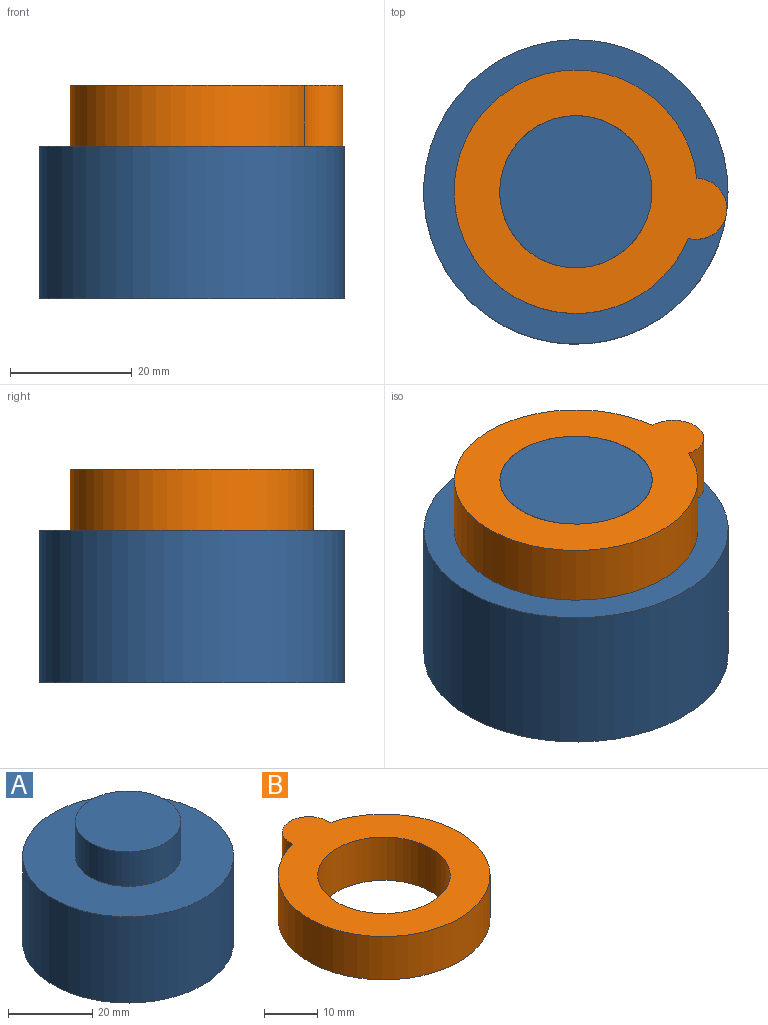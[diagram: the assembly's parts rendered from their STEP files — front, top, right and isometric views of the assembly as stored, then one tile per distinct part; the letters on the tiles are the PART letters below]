
ASSEMBLY  parts=2 mates=1
PART A: 5 faces, bbox 50x50x35 mm
  f0: cylinder r=25mm len=50mm, axis (0,0,-1), area 3927mm2, adj f1,f2
  f1: plane 50x50mm, normal (0,0,1), area 1472.6mm2, adj f0,f3
  f2: plane 50x50mm, normal (0,0,-1), area 1963.5mm2, adj f0
  f3: cylinder r=12.5mm len=25mm, axis (0,0,-1), area 785.4mm2, adj f1,f4
  f4: plane 25x25mm, normal (0,0,1), area 490.9mm2, adj f3
PART B: 5 faces, bbox 40x45x10 mm
  f0: cylinder r=20mm len=40mm, axis (0,0,-1), area 1156.4mm2, adj f1,f2,f4
  f1: plane 45x40mm, normal (0,0,1), area 807.1mm2, adj f0,f3,f4
  f2: plane 45x40mm, normal (0,0,-1), area 807.1mm2, adj f0,f3,f4
  f3: cylinder r=12.5mm len=25mm, axis (0,0,1), area 785.4mm2, adj f1,f2
  f4: cylinder r=5mm len=10mm, axis (0,0,1), area 169.6mm2, adj f0,f1,f2
PLACE A t=(-10.01,3.46,-3.65)mm fixed
PLACE B rot(axis=(0,0,-1),98.1deg) t=(-10.01,3.46,21.35)mm
MATE revolute A.f0 <-> B.f0  axis (0,0,-1) through (-10.01,3.46,26.35)mm
